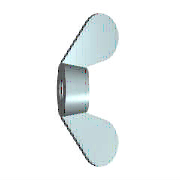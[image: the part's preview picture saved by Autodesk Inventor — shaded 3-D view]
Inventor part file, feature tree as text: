
AUTODESK INVENTOR PART (.ipt)
format: ipt  version: 2020 (Build 240168000, 168)  size: 172,544 bytes
history: native  units: mm (DEFAULTED — no unit token found)
features: sketch x2, extrude x1, mirror x1, hole x1, other x1, plane x1
ambient origin geometry x7: Origin, YZ Plane, XZ Plane, X Axis, Y Axis, Z Axis, Center Point
bodies: Solid1 (feature_tree), Body (feature_tree)
feature tree (7):
  sketch  "Sketch1"  dims[d0=12.5mm d1=14.0mm]
  extrude  "Wing1"  Depth=14.0mm
  mirror  "Wing2"
  hole  "Thread"  [1 undecoded]
  other  "Work Axis1"
  plane  "Work Plane1"
  sketch  "Sketch2"  dims[d2=13.5mm d3=6.0mm d57=90.0deg d4=10.0mm d5=16.0mm d6=2.8mm d7=0.0mm d8=0.933333mm d97=6.647mm d98=6.0mm d99=4.0mm d100=2.0mm d101=14.3117mm d102=8.0mm d103=20.594885mm d9=0.676582mm d10=30.0deg d11=0.0mm d108=0.0mm d109=0.676582mm d110=0.0mm d111=0.0mm d112=0.0mm]
note: 1 required parameter value undecoded (feature->parameter linkage not recoverable at this tier; creation-order binding heuristic only, values carry confidence <= 0.55)
